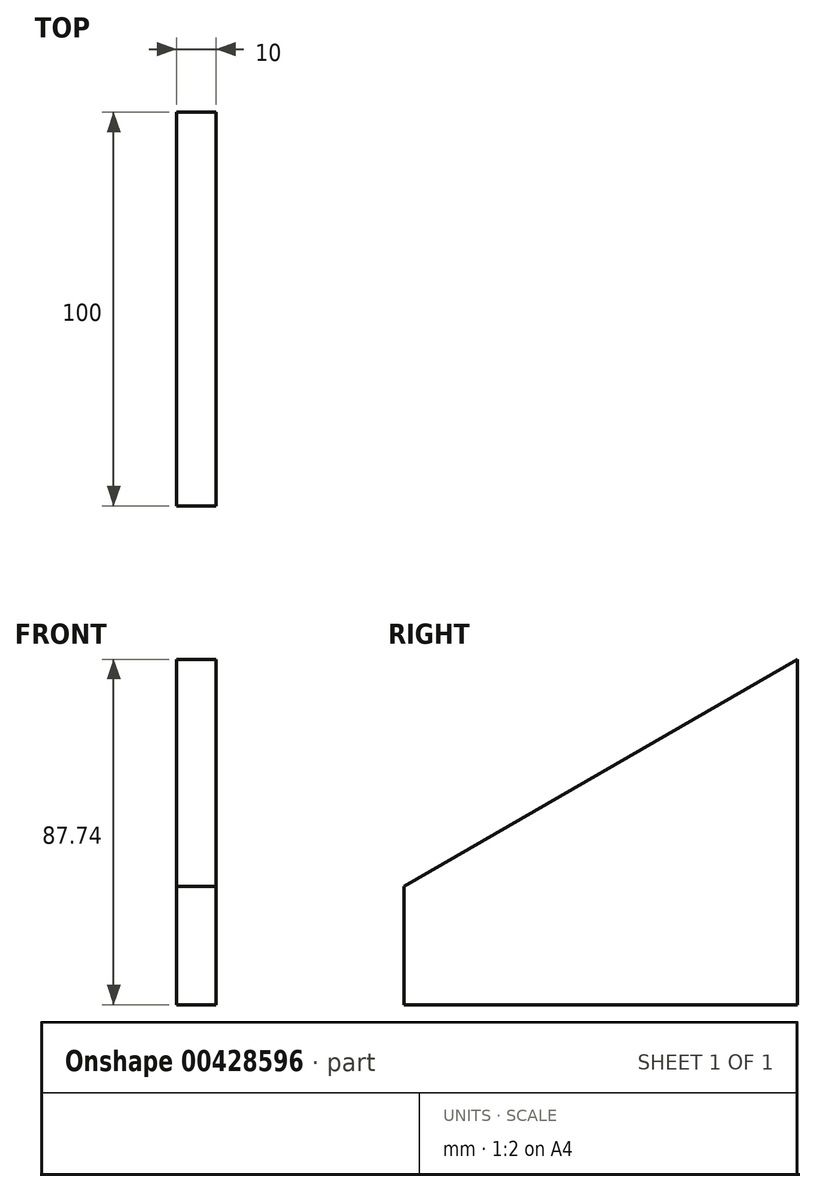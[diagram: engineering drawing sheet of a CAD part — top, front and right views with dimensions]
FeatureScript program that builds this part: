
annotation { "Feature Type Name" : "Feature", "Feature Type Description" : "" }
export const myFeature = defineFeature(function(context is Context, id is Id, definition is map)
    precondition{}
    {
        {
            var Q0;
            Q0=qCreatedBy(makeId("Right.planeOp"),FACE);
            var sketch = newSketch(context, id + "F0", { "sketchPlane" : qUnion([Q0])});
            skLineSegment(sketch, "E0.bottom", {"start": v(0, 0) * mm, "end": v(100, 0) * mm});
            skLineSegment(sketch, "E0.top", {"start": v(0, 30) * mm, "end": v(100, 30) * mm, "construction": true});
            skLineSegment(sketch, "E0.left", {"start": v(0, 0) * mm, "end": v(0, 30) * mm});
            skLineSegment(sketch, "E0.right", {"start": v(100, 0) * mm, "end": v(100, 30) * mm});
            skLineSegment(sketch, "E1", {"start": v(0, 30) * mm, "end": v(100, 87.74) * mm});
            skLineSegment(sketch, "E2", {"start": v(100, 87.74) * mm, "end": v(100, 30) * mm});
            skSolve(sketch);
        }
        {
            var Q0;
            Q0=makeQuery(id+"F0.imprint","IMPRINT",FACE,{"disambiguationData":[TD([[makeQuery(id+"F0.imprint","IMPRINT",EDGE,{"derivedFrom":sQuery(id+"F0.wireOp",EDGE,"E0.bottom")}),1.0]])]});
            extrude(context, id + "F1", {"entities" : qUnion([Q0]), "depth" : 10 * mm});
        }
    });
